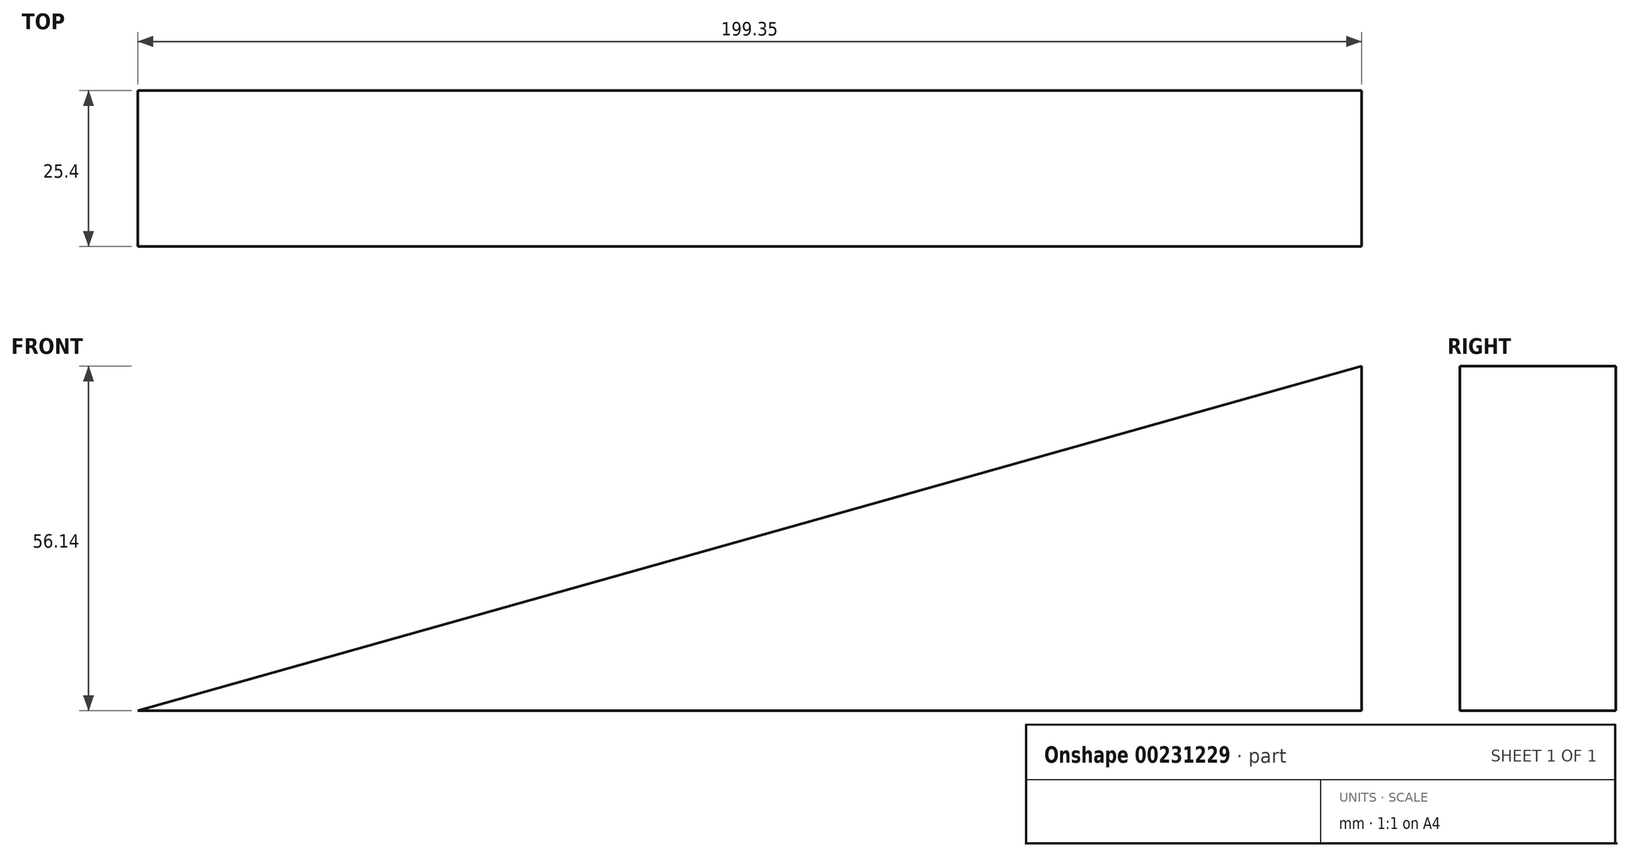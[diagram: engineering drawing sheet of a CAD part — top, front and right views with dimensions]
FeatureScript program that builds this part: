
annotation { "Feature Type Name" : "Feature", "Feature Type Description" : "" }
export const myFeature = defineFeature(function(context is Context, id is Id, definition is map)
    precondition{}
    {
        {
            var Q0;
            Q0=qCreatedBy(makeId("Front.planeOp"),FACE);
            var sketch = newSketch(context, id + "F0", { "sketchPlane" : qUnion([Q0])});
            skLineSegment(sketch, "E0", {"start": v(-99.54, 0) * mm, "end": v(99.8, 0) * mm});
            skLineSegment(sketch, "E1", {"start": v(99.8, 0) * mm, "end": v(99.8, 56.14) * mm});
            skLineSegment(sketch, "E2", {"start": v(99.8, 56.14) * mm, "end": v(-99.54, 0) * mm});
            skSolve(sketch);
        }
        {
            var Q0;
            Q0=makeQuery(id+"F0.imprint","IMPRINT",FACE,{"disambiguationData":[TD([[makeQuery(id+"F0.imprint","IMPRINT",EDGE,{"derivedFrom":sQuery(id+"F0.wireOp",EDGE,"E0")}),1.0]])]});
            extrude(context, id + "F1", {"entities" : qUnion([Q0]), "depth" : 25.4 * mm});
        }
    });
